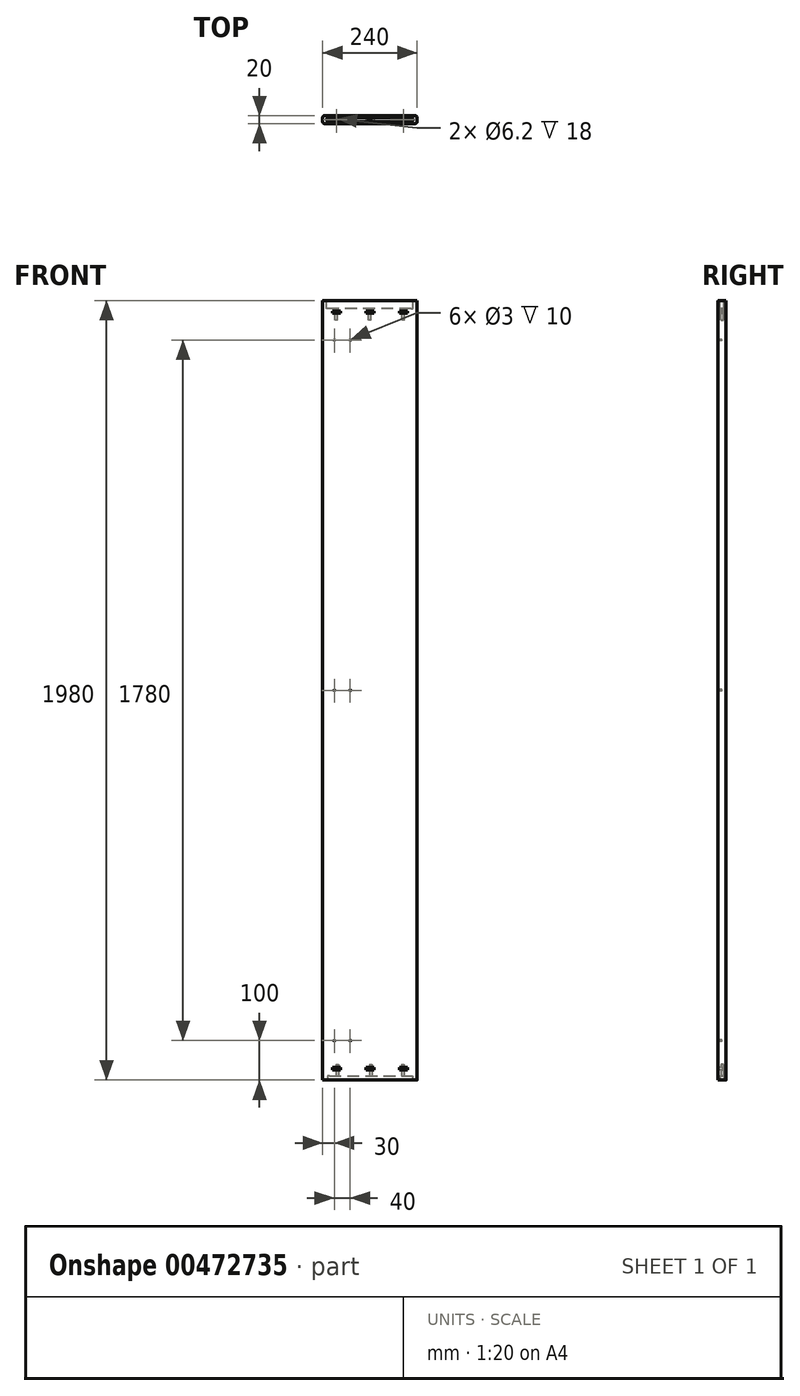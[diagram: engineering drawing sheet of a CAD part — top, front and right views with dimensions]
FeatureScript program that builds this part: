
annotation { "Feature Type Name" : "Feature", "Feature Type Description" : "" }
export const myFeature = defineFeature(function(context is Context, id is Id, definition is map)
    precondition{}
    {
        {
            var Q0;
            Q0=qCreatedBy(makeId("Front.planeOp"),FACE);
            var sketch = newSketch(context, id + "F0", { "sketchPlane" : qUnion([Q0])});
            skLineSegment(sketch, "E0.bottom", {"start": v(-120, -990) * mm, "end": v(120, -990) * mm});
            skLineSegment(sketch, "E0.top", {"start": v(-120, 990) * mm, "end": v(120, 990) * mm});
            skLineSegment(sketch, "E0.left", {"start": v(-120, -990) * mm, "end": v(-120, 990) * mm});
            skLineSegment(sketch, "E0.right", {"start": v(120, -990) * mm, "end": v(120, 990) * mm});
            skLineSegment(sketch, "E1", {"start": v(0, 990) * mm, "end": v(0, -990) * mm, "construction": true});
            skPoint(sketch, "E1.startSnap0", {"position": v(0, 990) * mm});
            skSolve(sketch);
        }
        {
            var Q0;
            Q0 = qSketchRegion(id + "F0", true);
            extrude(context, id + "F1", {"entities" : qUnion([Q0]), "depth" : 20 * mm});
        }
        {
            var Q0;
            Q0=makeQuery(id+"F1.opExtrude","CAP_FACE",FACE,{"disambiguationData":[OSD([sQuery(id+"F0.wireOp",EDGE,"E0.bottom"),sQuery(id+"F0.wireOp",EDGE,"E0.top"),sQuery(id+"F0.wireOp",EDGE,"E0.left"),sQuery(id+"F0.wireOp",EDGE,"E0.right")])],"isStart":false});
            var sketch = newSketch(context, id + "F2", { "sketchPlane" : qUnion([Q0])});
            skLineSegment(sketch, "E2", {"start": v(-90, 990) * mm, "end": v(-90, -990) * mm, "construction": true});
            skLineSegment(sketch, "E3", {"start": v(-90, 890) * mm, "end": v(-50, 890) * mm, "construction": true});
            skLineSegment(sketch, "E4", {"start": v(120, 0) * mm, "end": v(-120, 0) * mm, "construction": true});
            skCircle(sketch, "E5", {"center": v(-50, 890) * mm, "radius": 1.5 * mm});
            skCircle(sketch, "E6", {"center": v(-90, 890) * mm, "radius": 1.5 * mm});
            skCircle(sketch, "E7", {"center": v(-90, 0) * mm, "radius": 1.5 * mm});
            skCircle(sketch, "E8", {"center": v(-50, 0) * mm, "radius": 1.5 * mm});
            skCircle(sketch, "E9.MirrorC", {"center": v(-50, -890) * mm, "radius": 1.5 * mm});
            skCircle(sketch, "E10.MirrorC", {"center": v(-90, -890) * mm, "radius": 1.5 * mm});
            skLineSegment(sketch, "E11.MirrorCS", {"start": v(-90, -890) * mm, "end": v(-50, -890) * mm, "construction": true});
            skSolve(sketch);
        }
        {
            var Q0;
            Q0 = qSketchRegion(id + "F2", true);
            extrude(context, id + "F3", {"entities" : qUnion([Q0]), "operationType" : NewBodyOperationType.REMOVE, "oppositeDirection" : true, "depth" : 10 * mm, "offsetDistance" : 25 * mm});
        }
        {
            var Q0;
            Q0=makeQuery(id+"F1.opExtrude","SWEPT_FACE",FACE,{"disambiguationData":[OSD([sQuery(id+"F0.wireOp",EDGE,"E0.top")])]});
            var sketch = newSketch(context, id + "F4", { "sketchPlane" : qUnion([Q0])});
            skLineSegment(sketch, "E12", {"start": v(-120, -10) * mm, "end": v(120, -10) * mm, "construction": true});
            skLineSegment(sketch, "E13", {"start": v(0, 0) * mm, "end": v(0, -20) * mm, "construction": true});
            skArc(sketch, "E14", {"start": v(-105, -5) * mm, "mid": v(-110, -10) * mm, "end": v(-105, -15) * mm});
            skArc(sketch, "E15.MirrorC", {"start": v(105, -5) * mm, "mid": v(110, -10) * mm, "end": v(105, -15) * mm});
            skLineSegment(sketch, "E16", {"start": v(105, -5) * mm, "end": v(-105, -5) * mm});
            skLineSegment(sketch, "E17.MirrorCS", {"start": v(105, -15) * mm, "end": v(-105, -15) * mm});
            skSolve(sketch);
        }
        {
            var Q0;
            Q0 = qSketchRegion(id + "F4", true);
            extrude(context, id + "F5", {"entities" : qUnion([Q0]), "operationType" : NewBodyOperationType.REMOVE, "oppositeDirection" : true, "depth" : 20 * mm, "offsetDistance" : 25 * mm});
        }
        {
            var Q0;
            Q0=makeQuery(id+"F1.opExtrude","SWEPT_FACE",FACE,{"disambiguationData":[OSD([sQuery(id+"F0.wireOp",EDGE,"E0.bottom")])]});
            var sketch = newSketch(context, id + "F6", { "sketchPlane" : qUnion([Q0])});
            skLineSegment(sketch, "E18", {"start": v(120, 10) * mm, "end": v(-120, 10) * mm, "construction": true});
            skLineSegment(sketch, "E19", {"start": v(0, 0) * mm, "end": v(0, 20) * mm, "construction": true});
            skArc(sketch, "E20", {"start": v(103.04, 5) * mm, "mid": v(108.04, 10) * mm, "end": v(103.04, 15) * mm});
            skArc(sketch, "E21.MirrorC", {"start": v(-103.04, 5) * mm, "mid": v(-108.04, 10) * mm, "end": v(-103.04, 15) * mm});
            skLineSegment(sketch, "E22", {"start": v(-103.04, 5) * mm, "end": v(103.04, 5) * mm});
            skLineSegment(sketch, "E23.MirrorCS", {"start": v(-103.04, 15) * mm, "end": v(103.04, 15) * mm});
            skSolve(sketch);
        }
        {
            var Q0;
            Q0 = qSketchRegion(id + "F6", true);
            extrude(context, id + "F7", {"entities" : qUnion([Q0]), "operationType" : NewBodyOperationType.REMOVE, "oppositeDirection" : true, "depth" : 10 * mm, "offsetDistance" : 25 * mm});
        }
        {
            var Q0;
            Q0=makeQuery(id+"F1.opExtrude","CAP_EDGE",EDGE,{"disambiguationData":[OSD([sQuery(id+"F0.wireOp",EDGE,"E0.right")])],"isStart":true});
            var Q1;
            Q1=makeQuery(id+"F1.opExtrude","CAP_EDGE",EDGE,{"disambiguationData":[OSD([sQuery(id+"F0.wireOp",EDGE,"E0.right")])],"isStart":false});
            var Q2;
            Q2=makeQuery(id+"F1.opExtrude","CAP_EDGE",EDGE,{"disambiguationData":[OSD([sQuery(id+"F0.wireOp",EDGE,"E0.left")])],"isStart":false});
            var Q3;
            Q3=makeQuery(id+"F1.opExtrude","CAP_EDGE",EDGE,{"disambiguationData":[OSD([sQuery(id+"F0.wireOp",EDGE,"E0.left")])],"isStart":true});
            fillet(context, id + "F8", {"entities" : qUnion([Q0, Q1, Q2, Q3]), "radius" : 5 * mm, "tangentPropagation" : true, "allowEdgeOverflow" : false});
        }
        {
            var Q0;
            Q0=makeQuery(id+"F5.boolean.opBoolean","COPY",FACE,{"derivedFrom":makeQuery(id+"F5.opExtrude","CAP_FACE",FACE,{"disambiguationData":[OSD([sQuery(id+"F4.wireOp",EDGE,"E14"),sQuery(id+"F4.wireOp",EDGE,"E15.MirrorC"),sQuery(id+"F4.wireOp",EDGE,"E16"),sQuery(id+"F4.wireOp",EDGE,"E17.MirrorCS")])],"isStart":false})});
            var sketch = newSketch(context, id + "F9", { "sketchPlane" : qUnion([Q0])});
            skLineSegment(sketch, "E24", {"start": v(110, -10) * mm, "end": v(-110, -10) * mm, "construction": true});
            skCircle(sketch, "E25", {"center": v(85, -10) * mm, "radius": 3.1 * mm});
            skCircle(sketch, "E26", {"center": v(0, -10) * mm, "radius": 3.2 * mm});
            skCircle(sketch, "E27", {"center": v(-85, -10) * mm, "radius": 3.1 * mm});
            skSolve(sketch);
        }
        {
            var Q0;
            Q0 = qSketchRegion(id + "F9", true);
            extrude(context, id + "F10", {"entities" : qUnion([Q0]), "operationType" : NewBodyOperationType.REMOVE, "oppositeDirection" : true, "depth" : 30 * mm, "offsetDistance" : 25 * mm});
        }
        {
            var Q0;
            Q0=makeQuery(id+"F7.boolean.opBoolean","COPY",FACE,{"derivedFrom":makeQuery(id+"F7.opExtrude","CAP_FACE",FACE,{"disambiguationData":[OSD([sQuery(id+"F6.wireOp",EDGE,"E20"),sQuery(id+"F6.wireOp",EDGE,"E21.MirrorC"),sQuery(id+"F6.wireOp",EDGE,"E22"),sQuery(id+"F6.wireOp",EDGE,"E23.MirrorCS")])],"isStart":false})});
            var sketch = newSketch(context, id + "F11", { "sketchPlane" : qUnion([Q0])});
            skLineSegment(sketch, "E28", {"start": v(108.04, 10) * mm, "end": v(-108.04, 10) * mm, "construction": true});
            skCircle(sketch, "E29", {"center": v(83.04, 10) * mm, "radius": 3.1 * mm});
            skCircle(sketch, "E30", {"center": v(1.96, 10) * mm, "radius": 3.1 * mm});
            skCircle(sketch, "E31", {"center": v(-83.04, 10) * mm, "radius": 3.1 * mm});
            skSolve(sketch);
        }
        {
            var Q0;
            Q0 = qSketchRegion(id + "F11", true);
            extrude(context, id + "F12", {"entities" : qUnion([Q0]), "operationType" : NewBodyOperationType.REMOVE, "oppositeDirection" : true, "depth" : 30 * mm, "offsetDistance" : 25 * mm});
        }
        {
            var Q0;
            Q0=makeQuery(id+"F1.opExtrude","CAP_FACE",FACE,{"disambiguationData":[OSD([sQuery(id+"F0.wireOp",EDGE,"E0.bottom"),sQuery(id+"F0.wireOp",EDGE,"E0.top"),sQuery(id+"F0.wireOp",EDGE,"E0.left"),sQuery(id+"F0.wireOp",EDGE,"E0.right")])],"isStart":false});
            var sketch = newSketch(context, id + "F13", { "sketchPlane" : qUnion([Q0])});
            skLineSegment(sketch, "E32.0", {"start": v(105, 970) * mm, "end": v(-105, 970) * mm, "construction": true});
            skLineSegment(sketch, "E33.0", {"start": v(95, 958) * mm, "end": v(75, 958) * mm});
            skLineSegment(sketch, "E34.0", {"start": v(95, 964) * mm, "end": v(75, 964) * mm});
            skLineSegment(sketch, "E35", {"start": v(0, 958) * mm, "end": v(0, 964) * mm, "construction": true});
            skLineSegment(sketch, "E36", {"start": v(105, 970) * mm, "end": v(105, 958) * mm, "construction": true});
            skLineSegment(sketch, "E37", {"start": v(-105, 970) * mm, "end": v(-105, 958) * mm, "construction": true});
            skLineSegment(sketch, "E38.0", {"start": v(85, 964) * mm, "end": v(85, 958) * mm, "construction": true});
            skLineSegment(sketch, "E39.0", {"start": v(-85, 964) * mm, "end": v(-85, 958) * mm, "construction": true});
            skLineSegment(sketch, "E40.0", {"start": v(75, 964) * mm, "end": v(75, 958) * mm});
            skLineSegment(sketch, "E41.0", {"start": v(95, 964) * mm, "end": v(95, 958) * mm});
            skLineSegment(sketch, "E42.0", {"start": v(-10, 958) * mm, "end": v(-10, 964) * mm});
            skLineSegment(sketch, "E43.0", {"start": v(9.9, 958) * mm, "end": v(9.9, 964) * mm});
            skLineSegment(sketch, "E44.0", {"start": v(-95, 964) * mm, "end": v(-95, 958) * mm});
            skLineSegment(sketch, "E45.0", {"start": v(-75, 964) * mm, "end": v(-75, 958) * mm});
            skLineSegment(sketch, "E46", {"start": v(-115, 0) * mm, "end": v(115, 0) * mm, "construction": true});
            skPoint(sketch, "E47.orphan", {"position": v(105, 964) * mm});
            skLineSegment(sketch, "E48.trimOffspring", {"start": v(9.9, 958) * mm, "end": v(-10, 958) * mm});
            skLineSegment(sketch, "E49.trimOffspring", {"start": v(9.9, 964) * mm, "end": v(-10, 964) * mm});
            skLineSegment(sketch, "E50.trimOffspring", {"start": v(-75, 958) * mm, "end": v(-95, 958) * mm});
            skLineSegment(sketch, "E51.trimOffspring", {"start": v(-75, 964) * mm, "end": v(-95, 964) * mm});
            skPoint(sketch, "E52.orphan", {"position": v(-105, 964) * mm});
            skLineSegment(sketch, "E53.MirrorCS", {"start": v(-75, -964) * mm, "end": v(-75, -958) * mm});
            skLineSegment(sketch, "E54.MirrorCS", {"start": v(-10, -958) * mm, "end": v(-10, -964) * mm});
            skLineSegment(sketch, "E55.MirrorCS", {"start": v(95, -964) * mm, "end": v(95, -958) * mm});
            skLineSegment(sketch, "E56.MirrorCS", {"start": v(75, -964) * mm, "end": v(75, -958) * mm});
            skLineSegment(sketch, "E57.MirrorCS", {"start": v(9.9, -958) * mm, "end": v(9.9, -964) * mm});
            skLineSegment(sketch, "E58.MirrorCS", {"start": v(-95, -964) * mm, "end": v(-95, -958) * mm});
            skLineSegment(sketch, "E59.MirrorCS", {"start": v(-75, -958) * mm, "end": v(-95, -958) * mm});
            skLineSegment(sketch, "E60.MirrorCS", {"start": v(9.9, -958) * mm, "end": v(-10, -958) * mm});
            skLineSegment(sketch, "E61.MirrorCS", {"start": v(95, -964) * mm, "end": v(75, -964) * mm});
            skLineSegment(sketch, "E62.MirrorCS", {"start": v(0, -958) * mm, "end": v(0, -964) * mm, "construction": true});
            skLineSegment(sketch, "E63.MirrorCS", {"start": v(95, -958) * mm, "end": v(75, -958) * mm});
            skLineSegment(sketch, "E64.MirrorCS", {"start": v(-85, -964) * mm, "end": v(-85, -958) * mm, "construction": true});
            skLineSegment(sketch, "E65.MirrorCS", {"start": v(85, -964) * mm, "end": v(85, -958) * mm, "construction": true});
            skLineSegment(sketch, "E66.MirrorCS", {"start": v(9.9, -964) * mm, "end": v(-10, -964) * mm});
            skLineSegment(sketch, "E67.MirrorCS", {"start": v(-75, -964) * mm, "end": v(-95, -964) * mm});
            skSolve(sketch);
        }
        {
            var Q0;
            Q0 = qSketchRegion(id + "F13", true);
            extrude(context, id + "F14", {"entities" : qUnion([Q0]), "operationType" : NewBodyOperationType.REMOVE, "oppositeDirection" : true, "depth" : 17 * mm, "offsetDistance" : 25 * mm});
        }
    });
